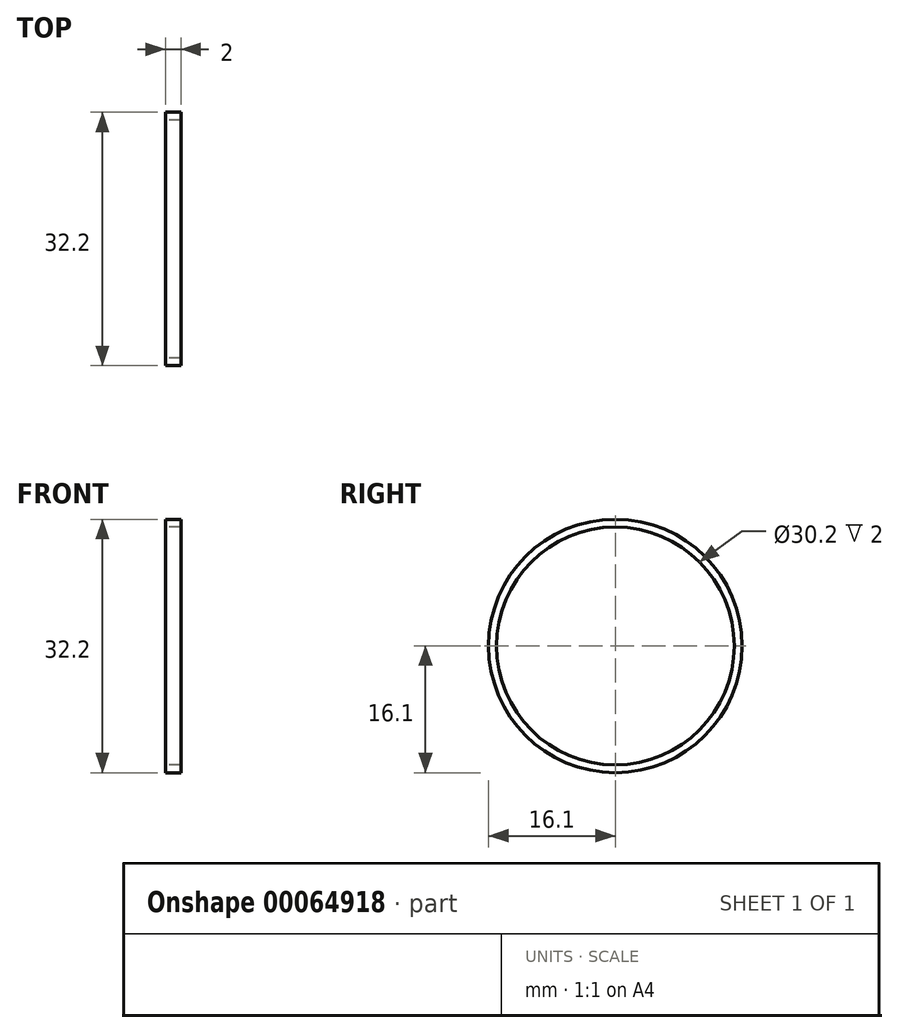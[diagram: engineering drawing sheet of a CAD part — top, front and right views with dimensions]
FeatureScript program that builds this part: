
annotation { "Feature Type Name" : "Feature", "Feature Type Description" : "" }
export const myFeature = defineFeature(function(context is Context, id is Id, definition is map)
    precondition{}
    {
        {
            var Q0;
            Q0=qCreatedBy(makeId("Right.planeOp"),FACE);
            var sketch = newSketch(context, id + "F0", { "sketchPlane" : qUnion([Q0])});
            skCircle(sketch, "E0", {"center": v(0, 0) * mm, "radius": 16.1 * mm});
            skCircle(sketch, "E1.0", {"center": v(0, 0) * mm, "radius": 15.1 * mm});
            skSolve(sketch);
        }
        {
            var Q0;
            Q0=makeQuery(id+"F0.imprint","IMPRINT",FACE,{"disambiguationData":[TD([[makeQuery(id+"F0.imprint","IMPRINT",EDGE,{"derivedFrom":sQuery(id+"F0.wireOp",EDGE,"E0")}),1.0]])]});
            extrude(context, id + "F1", {"entities" : qUnion([Q0]), "depth" : 2 * mm});
        }
    });
